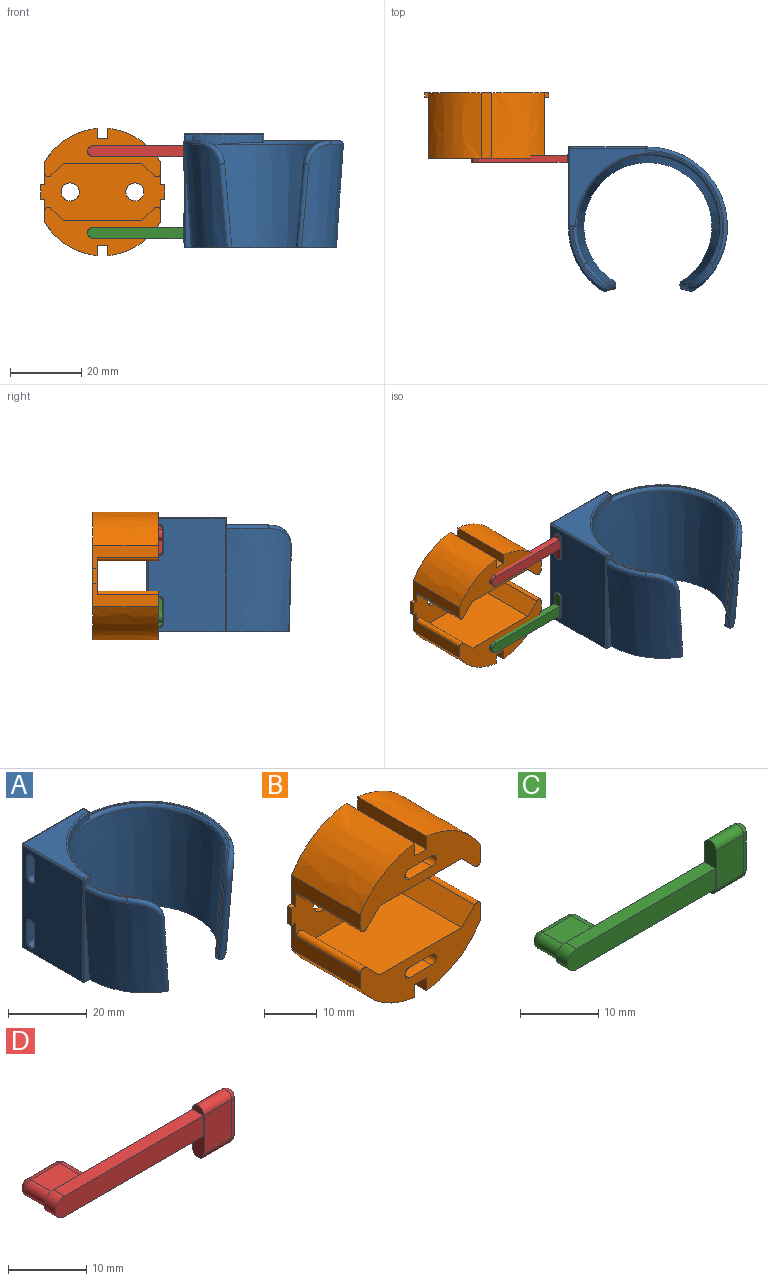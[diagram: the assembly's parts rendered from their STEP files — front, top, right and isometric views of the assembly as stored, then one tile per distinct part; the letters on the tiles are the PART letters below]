
ASSEMBLY  parts=4 mates=4
PART A: 68 faces, bbox 48.5x44.2x103.8 mm
  f0: plane 23.82x1.59mm, normal (0,-1,0), area 19mm2, adj f3,f4,f40
  f1: plane 24.08x1.61mm, normal (1,0,0), area 19.4mm2, adj f4,f7,f53
  f2: plane 32.72x21.33mm, normal (0,0,1), area 17.7mm2, adj f11,f13,f34,f37
  f3: cone r=20.4mm half-angle=3.8deg, axis (0,0,1), area 585.5mm2, adj f0,f4,f31,f32,f33,f41
  f4: plane 42.91x39.75mm, normal (0,0,-1), area 409mm2, adj f0,f1,f3,f5,f7,f8,f9,f14
  f5: cone r=20mm half-angle=3.8deg, axis (0,0,1), area 2760.2mm2, adj f4,f12,f28,f29,f30,f34,f35,f36
  f6: plane 11.39x3.3mm, normal (0,0,1), area 4.6mm2, adj f10,f15,f28,f31
  f7: cone r=20.4mm half-angle=3.8deg, axis (0,0,1), area 1556.4mm2, adj f1,f4,f37,f38,f39,f56
  f8: plane 23.63x2.15mm, normal (-1,0,0.09), area 11.2mm2, adj f4,f11,f36,f39
  f9: plane 23.63x2.15mm, normal (1,0,0.09), area 11.2mm2, adj f4,f10,f30,f33
  f10: cylinder r=7mm len=6.97mm, axis (0,1,0), area 5.8mm2, adj f6,f9,f29,f32
  f11: cylinder r=7mm len=6.97mm, axis (0,1,0), area 5.8mm2, adj f2,f8,f35,f38
  f12: cylinder r=20.45mm len=20.16mm, axis (0,0,-1), area 76.5mm2, adj f5,f15,f28,f34,f46,f47
  f13: plane 1.93x1.45mm, normal (1,0,0), area 2.5mm2, adj f2,f34,f37,f46,f54,f59
  f14: plane 31.6x21.8mm, normal (-1,0,0), area 637.3mm2, adj f4,f40,f41,f42,f43,f48,f49,f60
  f15: plane 2.4x2.02mm, normal (0,-1,0), area 3.6mm2, adj f6,f12,f28,f31,f43,f44
  f16: plane 31.2x21.76mm, normal (0,1,0), area 674mm2, adj f49,f50,f53,f55,f56,f58,f59
  f17: plane 21.61x21.59mm, normal (0,0,1), area 156.8mm2, adj f44,f47,f48,f54,f55
  f18: cylinder r=1.2mm len=6.8mm, axis (-1,0,0), area 25.6mm2, adj f19,f21,f22,f64
  f19: plane 6.8x6mm, normal (0,-1,0), area 40.8mm2, adj f18,f20,f22,f65
  f20: cylinder r=1.2mm len=6.8mm, axis (-1,0,0), area 25.6mm2, adj f19,f21,f22,f67
  f21: plane 6.8x6mm, normal (0,1,0), area 40.8mm2, adj f18,f20,f22,f66
  f22: plane 8.4x2.4mm, normal (-1,0,0), area 18.9mm2, adj f18,f19,f20,f21
  f23: cylinder r=1.2mm len=6.8mm, axis (-1,0,0), area 25.6mm2, adj f24,f26,f27,f60
  f24: plane 6.8x6mm, normal (0,-1,0), area 40.8mm2, adj f23,f25,f27,f61
  f25: cylinder r=1.2mm len=6.8mm, axis (-1,0,0), area 25.6mm2, adj f24,f26,f27,f63
  f26: plane 6.8x6mm, normal (0,1,0), area 40.8mm2, adj f23,f25,f27,f62
  f27: plane 8.4x2.4mm, normal (-1,0,0), area 18.9mm2, adj f23,f24,f25,f26
  f28: torus R=20.94mm, axis (0,0,-1), area 16.6mm2, adj f5,f6,f12,f15,f29
  f29: bspline ~8.23x8.08mm, area 13.4mm2, adj f5,f10,f28,f30
  f30: bspline ~23.61x2.47mm, area 23.1mm2, adj f4,f5,f9,f29
  f31: torus R=21.33mm, axis (0,0,-1), area 20.3mm2, adj f3,f6,f15,f32,f42
  f32: bspline ~9.36x8.94mm, area 24.7mm2, adj f3,f10,f31,f33
  f33: bspline ~103.7x10.73mm, area 50.5mm2, adj f3,f4,f9,f32
  f34: torus R=20.94mm, axis (0,0,-1), area 68.7mm2, adj f2,f5,f12,f13,f35,f46
  f35: bspline ~8.23x8.08mm, area 13.4mm2, adj f5,f11,f34,f36
  f36: bspline ~23.61x2.47mm, area 23.1mm2, adj f4,f5,f8,f35
  f37: torus R=21.33mm, axis (0,0,-1), area 76.8mm2, adj f2,f7,f13,f38,f58
  f38: bspline ~9.36x8.94mm, area 24.7mm2, adj f7,f11,f37,f39
  f39: bspline ~103.7x10.73mm, area 50.5mm2, adj f4,f7,f8,f38
  f40: cylinder r=0.4mm len=23.82mm, axis (0,0,1), area 15mm2, adj f0,f4,f14,f41
  f41: bspline ~6.62x0.47mm, area 2.3mm2, adj f3,f14,f40,f42
  f42: bspline ~0.82x0.4mm, area 0.3mm2, adj f14,f31,f41,f43
  f43: cylinder r=0.4mm len=1.92mm, axis (0,0,1), area 1.2mm2, adj f14,f15,f42,f45
  f44: cylinder r=0.4mm len=2.02mm, axis (-1,0,0), area 1.1mm2, adj f15,f17,f45,f47
  f45: sphere r=0.4mm, area 0.3mm2, adj f43,f44,f48
  f46: cylinder r=0.4mm len=2.03mm, axis (0,0,-1), area 1.2mm2, adj f12,f13,f34,f51
  f47: torus R=20.85mm, axis (0,0,1), area 19.5mm2, adj f12,f17,f44,f51
  f48: cylinder r=0.4mm len=21.61mm, axis (0,1,0), area 13.6mm2, adj f14,f17,f45,f52
  f49: cylinder r=0.4mm len=31.6mm, axis (0,0,-1), area 19.7mm2, adj f14,f16,f50,f52
  f50: cylinder r=0.4mm len=22.39mm, axis (-1,0,0), area 13.8mm2, adj f4,f16,f49,f53
  f51: sphere r=0.4mm, area 0.2mm2, adj f46,f47,f54
  f52: sphere r=0.4mm, area 0.3mm2, adj f48,f49,f55
  f53: cylinder r=0.4mm len=24.08mm, axis (0,0,1), area 15mm2, adj f1,f16,f50,f56
  f54: cylinder r=0.4mm len=1.45mm, axis (0,-1,0), area 0.9mm2, adj f13,f17,f51,f57
  f55: cylinder r=0.4mm len=21.59mm, axis (1,0,0), area 13.6mm2, adj f16,f17,f52,f57
  f56: bspline ~5.3x0.41mm, area 2.2mm2, adj f7,f16,f53,f58
  f57: sphere r=0.4mm, area 0.3mm2, adj f54,f55,f59
  f58: bspline ~1.03x0.47mm, area 0.3mm2, adj f16,f37,f56,f59
  f59: cylinder r=0.4mm len=1.93mm, axis (0,0,1), area 1.2mm2, adj f13,f16,f57,f58
  f60: torus R=1.4mm, axis (1,0,0), area 1.3mm2, adj f14,f23,f61,f62
  f61: cylinder r=0.2mm len=6mm, axis (0,0,-1), area 1.9mm2, adj f14,f24,f60,f63
  f62: cylinder r=0.2mm len=6mm, axis (0,0,1), area 1.9mm2, adj f14,f26,f60,f63
  f63: torus R=1.4mm, axis (1,0,0), area 1.3mm2, adj f14,f25,f61,f62
  f64: torus R=1.4mm, axis (1,0,0), area 1.3mm2, adj f14,f18,f65,f66
  f65: cylinder r=0.2mm len=6mm, axis (0,0,-1), area 1.9mm2, adj f14,f19,f64,f67
  f66: cylinder r=0.2mm len=6mm, axis (0,0,1), area 1.9mm2, adj f14,f21,f64,f67
  f67: torus R=1.4mm, axis (1,0,0), area 1.3mm2, adj f14,f20,f65,f66
PART B: 46 faces, bbox 34.8x18.4x35.9 mm
  f0: plane 32.4x13.71mm, normal (0,-1,0), area 227.9mm2, adj f8,f9,f15,f16,f17,f18,f19,f20
  f1: plane 4x1.2mm, normal (-1,0,0), area 4.8mm2, adj f2,f11,f13,f14
  f2: plane 1.2x1.2mm, normal (0,0,-1), area 1.4mm2, adj f1,f3,f13,f14
  f3: plane 18.4x6.58mm, normal (-1,0,0), area 65.7mm2, adj f2,f13,f14,f26,f31,f33
  f4: plane 18.4x6.58mm, normal (1,0,0), area 65.7mm2, adj f5,f13,f14,f30,f31,f32
  f5: plane 1.2x1.2mm, normal (0,0,-1), area 1.4mm2, adj f4,f6,f13,f14
  f6: plane 4x1.2mm, normal (1,0,0), area 4.8mm2, adj f5,f7,f13,f14
  f7: plane 1.2x1.2mm, normal (0,0,1), area 1.4mm2, adj f6,f8,f13,f14
  f8: plane 18.4x6.58mm, normal (1,0,0), area 65.7mm2, adj f0,f7,f13,f14,f18,f34
  f9: plane 18.4x6.58mm, normal (-1,0,0), area 65.7mm2, adj f0,f11,f13,f14,f22,f35
  f10: cylinder r=2.53mm len=5.07mm, axis (0,1,0), area 19.1mm2, adj f13,f14
  f11: plane 1.2x1.2mm, normal (0,0,1), area 1.4mm2, adj f1,f9,f13,f14
  f12: cylinder r=2.53mm len=5.07mm, axis (0,1,0), area 19.1mm2, adj f13,f14
  f13: plane 34.8x16mm, normal (0,-1,0), area 438.5mm2, adj f1,f2,f3,f4,f5,f6,f7,f8
  f14: plane 35.85x34.8mm, normal (0,1,0), area 932.2mm2, adj f1,f2,f3,f4,f5,f6,f7,f8
  f15: plane 17.2x3.49mm, normal (-0.71,0,-0.71), area 85mm2, adj f0,f13,f16,f34
  f16: plane 22x17.2mm, normal (0,0,-1), area 378.4mm2, adj f0,f13,f15,f17
  f17: plane 17.2x3.49mm, normal (0.71,0,-0.71), area 85mm2, adj f0,f13,f16,f35
  f18: extruded ~18.4x14.7mm, area 331.8mm2, adj f0,f8,f14,f19
  f19: plane 18.4x3mm, normal (-1,0,0), area 55.2mm2, adj f0,f14,f18,f20
  f20: plane 18.4x3mm, normal (0,0,1), area 55.2mm2, adj f0,f14,f19,f21
  f21: plane 18.4x3mm, normal (1,0,0), area 55.2mm2, adj f0,f14,f20,f22
  f22: extruded ~18.4x14.7mm, area 331.8mm2, adj f0,f9,f14,f21
  f23: plane 17.2x3.49mm, normal (0.71,0,0.71), area 85mm2, adj f13,f24,f31,f33
  f24: plane 22x17.2mm, normal (0,0,1), area 378.4mm2, adj f13,f23,f25,f31
  f25: plane 17.2x3.49mm, normal (-0.71,0,0.71), area 85mm2, adj f13,f24,f31,f32
  f26: extruded ~18.4x14.7mm, area 331.8mm2, adj f3,f14,f27,f31
  f27: plane 18.4x3mm, normal (1,0,0), area 55.2mm2, adj f14,f26,f28,f31
  f28: plane 18.4x3mm, normal (0,0,-1), area 55.2mm2, adj f14,f27,f29,f31
  f29: plane 18.4x3mm, normal (-1,0,0), area 55.2mm2, adj f14,f28,f30,f31
  f30: extruded ~18.4x14.7mm, area 331.8mm2, adj f4,f14,f29,f31
  f31: plane 32.4x13.71mm, normal (0,-1,0), area 227.9mm2, adj f3,f4,f23,f24,f25,f26,f27,f28
  f32: cylinder r=1mm len=17.2mm, axis (0,1,0), area 40.5mm2, adj f4,f13,f25,f31
  f33: cylinder r=1mm len=17.2mm, axis (0,1,0), area 40.5mm2, adj f3,f13,f23,f31
  f34: cylinder r=1mm len=17.2mm, axis (0,1,0), area 40.5mm2, adj f0,f8,f13,f15
  f35: cylinder r=1mm len=17.2mm, axis (0,-1,0), area 40.5mm2, adj f0,f9,f13,f17
  f36: cylinder r=1.2mm len=6mm, axis (0,-1,0), area 22.6mm2, adj f31,f37,f39,f40
  f37: plane 6x6mm, normal (0,0,1), area 36mm2, adj f31,f36,f38,f40
  f38: cylinder r=1.2mm len=6mm, axis (0,-1,0), area 22.6mm2, adj f31,f37,f39,f40
  f39: plane 6x6mm, normal (0,0,-1), area 36mm2, adj f31,f36,f38,f40
  f40: plane 8.4x2.4mm, normal (0,-1,0), area 18.9mm2, adj f36,f37,f38,f39
  f41: cylinder r=1.2mm len=6mm, axis (0,-1,0), area 22.6mm2, adj f0,f42,f44,f45
  f42: plane 6x6mm, normal (0,0,1), area 36mm2, adj f0,f41,f43,f45
  f43: cylinder r=1.2mm len=6mm, axis (0,-1,0), area 22.6mm2, adj f0,f42,f44,f45
  f44: plane 6x6mm, normal (0,0,-1), area 36mm2, adj f0,f41,f43,f45
  f45: plane 8.4x2.4mm, normal (0,-1,0), area 18.9mm2, adj f41,f42,f43,f44
PART C: 28 faces, bbox 32.9x7.1x8.1 mm
  f0: plane 26.8x3.2mm, normal (0,-1,0), area 84.7mm2, adj f7,f8,f9,f10
  f1: plane 26.8x3.2mm, normal (0,1,0), area 63.9mm2, adj f7,f8,f9,f10,f20,f21,f22,f23
  f2: cylinder r=1.2mm len=3.8mm, axis (0,-1,0), area 14.3mm2, adj f3,f5,f18,f22
  f3: plane 5.2x3.8mm, normal (0,0,1), area 19.8mm2, adj f2,f4,f16,f20
  f4: cylinder r=1.2mm len=3.8mm, axis (0,-1,0), area 14.3mm2, adj f3,f5,f17,f21
  f5: plane 5.2x3.8mm, normal (0,0,-1), area 19.8mm2, adj f2,f4,f19,f23
  f6: plane 5.6x0.4mm, normal (0,1,0), area 2.2mm2, adj f16,f17,f18,f19
  f7: plane 8.1x2.1mm, normal (-1,0,0), area 9.7mm2, adj f0,f1,f8,f10,f11,f12,f13,f14
  f8: plane 25.2x2mm, normal (0,0,1), area 50.4mm2, adj f0,f1,f7,f9
  f9: cylinder r=1.6mm len=3.2mm, axis (0,1,0), area 10.1mm2, adj f0,f1,f8,f10
  f10: plane 25.2x2mm, normal (0,0,-1), area 50.4mm2, adj f0,f1,f7,f9
  f11: plane 6x5mm, normal (0,1,0), area 30mm2, adj f7,f12,f14,f24
  f12: cylinder r=1.05mm len=5mm, axis (1,0,0), area 16.5mm2, adj f7,f11,f13,f25
  f13: plane 6x5mm, normal (0,-1,0), area 30mm2, adj f7,f12,f14,f27
  f14: cylinder r=1.05mm len=5mm, axis (1,0,0), area 16.5mm2, adj f7,f11,f13,f26
  f15: plane 6.1x0.1mm, normal (1,0,0), area 0.6mm2, adj f24,f25,f26,f27
  f16: cylinder r=1mm len=5.2mm, axis (1,0,0), area 8.2mm2, adj f3,f6,f17,f18
  f17: torus R=0.2mm, axis (0,-1,0), area 4.1mm2, adj f4,f6,f16,f19
  f18: torus R=0.2mm, axis (0,-1,0), area 4.1mm2, adj f2,f6,f16,f19
  f19: cylinder r=1mm len=5.2mm, axis (-1,0,0), area 8.2mm2, adj f5,f6,f17,f18
  f20: cylinder r=0.2mm len=5.2mm, axis (-1,0,0), area 1.6mm2, adj f1,f3,f21,f22
  f21: torus R=1.4mm, axis (0,-1,0), area 1.3mm2, adj f1,f4,f20,f23
  f22: torus R=1.4mm, axis (0,-1,0), area 1.3mm2, adj f1,f2,f20,f23
  f23: cylinder r=0.2mm len=5.2mm, axis (1,0,0), area 1.6mm2, adj f1,f5,f21,f22
  f24: cylinder r=1mm len=6mm, axis (0,0,-1), area 9.4mm2, adj f11,f15,f25,f26
  f25: torus R=0.05mm, axis (-1,0,0), area 3.4mm2, adj f12,f15,f24,f27
  f26: torus R=0.05mm, axis (-1,0,0), area 3.4mm2, adj f14,f15,f24,f27
  f27: cylinder r=1mm len=6mm, axis (0,0,1), area 9.4mm2, adj f13,f15,f25,f26
PART D: 28 faces, bbox 32.9x7.1x8.1 mm
  f0: plane 26.8x3.2mm, normal (0,-1,0), area 84.7mm2, adj f7,f8,f9,f10
  f1: plane 26.8x3.2mm, normal (0,1,0), area 63.9mm2, adj f7,f8,f9,f10,f20,f21,f22,f23
  f2: cylinder r=1.2mm len=3.8mm, axis (0,-1,0), area 14.3mm2, adj f3,f5,f18,f22
  f3: plane 5.2x3.8mm, normal (0,0,-1), area 19.8mm2, adj f2,f4,f16,f20
  f4: cylinder r=1.2mm len=3.8mm, axis (0,-1,0), area 14.3mm2, adj f3,f5,f17,f21
  f5: plane 5.2x3.8mm, normal (0,0,1), area 19.8mm2, adj f2,f4,f19,f23
  f6: plane 5.6x0.4mm, normal (0,1,0), area 2.2mm2, adj f16,f17,f18,f19
  f7: plane 8.1x2.1mm, normal (-1,0,0), area 9.7mm2, adj f0,f1,f8,f10,f11,f12,f13,f14
  f8: plane 25.2x2mm, normal (0,0,-1), area 50.4mm2, adj f0,f1,f7,f9
  f9: cylinder r=1.6mm len=3.2mm, axis (0,1,0), area 10.1mm2, adj f0,f1,f8,f10
  f10: plane 25.2x2mm, normal (0,0,1), area 50.4mm2, adj f0,f1,f7,f9
  f11: plane 6x5mm, normal (0,1,0), area 30mm2, adj f7,f12,f14,f24
  f12: cylinder r=1.05mm len=5mm, axis (1,0,0), area 16.5mm2, adj f7,f11,f13,f25
  f13: plane 6x5mm, normal (0,-1,0), area 30mm2, adj f7,f12,f14,f27
  f14: cylinder r=1.05mm len=5mm, axis (1,0,0), area 16.5mm2, adj f7,f11,f13,f26
  f15: plane 6.1x0.1mm, normal (1,0,0), area 0.6mm2, adj f24,f25,f26,f27
  f16: cylinder r=1mm len=5.2mm, axis (1,0,0), area 8.2mm2, adj f3,f6,f17,f18
  f17: torus R=0.2mm, axis (0,-1,0), area 4.1mm2, adj f4,f6,f16,f19
  f18: torus R=0.2mm, axis (0,-1,0), area 4.1mm2, adj f2,f6,f16,f19
  f19: cylinder r=1mm len=5.2mm, axis (-1,0,0), area 8.2mm2, adj f5,f6,f17,f18
  f20: cylinder r=0.2mm len=5.2mm, axis (-1,0,0), area 1.6mm2, adj f1,f3,f21,f22
  f21: torus R=1.4mm, axis (0,-1,0), area 1.3mm2, adj f1,f4,f20,f23
  f22: torus R=1.4mm, axis (0,-1,0), area 1.3mm2, adj f1,f2,f20,f23
  f23: cylinder r=0.2mm len=5.2mm, axis (1,0,0), area 1.6mm2, adj f1,f5,f21,f22
  f24: cylinder r=1mm len=6mm, axis (0,0,1), area 9.4mm2, adj f11,f15,f25,f26
  f25: torus R=0.05mm, axis (-1,0,0), area 3.4mm2, adj f12,f15,f24,f27
  f26: torus R=0.05mm, axis (-1,0,0), area 3.4mm2, adj f14,f15,f24,f27
  f27: cylinder r=1mm len=6mm, axis (0,0,-1), area 9.4mm2, adj f13,f15,f25,f26
PLACE A t=(97.52,-61.11,16.53)mm
PLACE B t=(64.92,-23.54,32.13)mm fixed
PLACE C t=(52.23,-41.06,20.67)mm
PLACE D t=(52.63,-41.06,62.19)mm
MATE slider B.f40 <-> C.f6  axis (0,-1,0) through (52.23,-35.94,20.67)mm
MATE slider C.f15 <-> A.f27  axis (1,0,0) through (80.83,-42.06,22.05)mm
MATE slider A.f22 <-> D.f15  axis (-1,0,0) through (82.13,-42.06,42.22)mm
MATE slider B.f45 <-> D.f6  axis (0,-1,0) through (52.23,-35.94,43.59)mm
